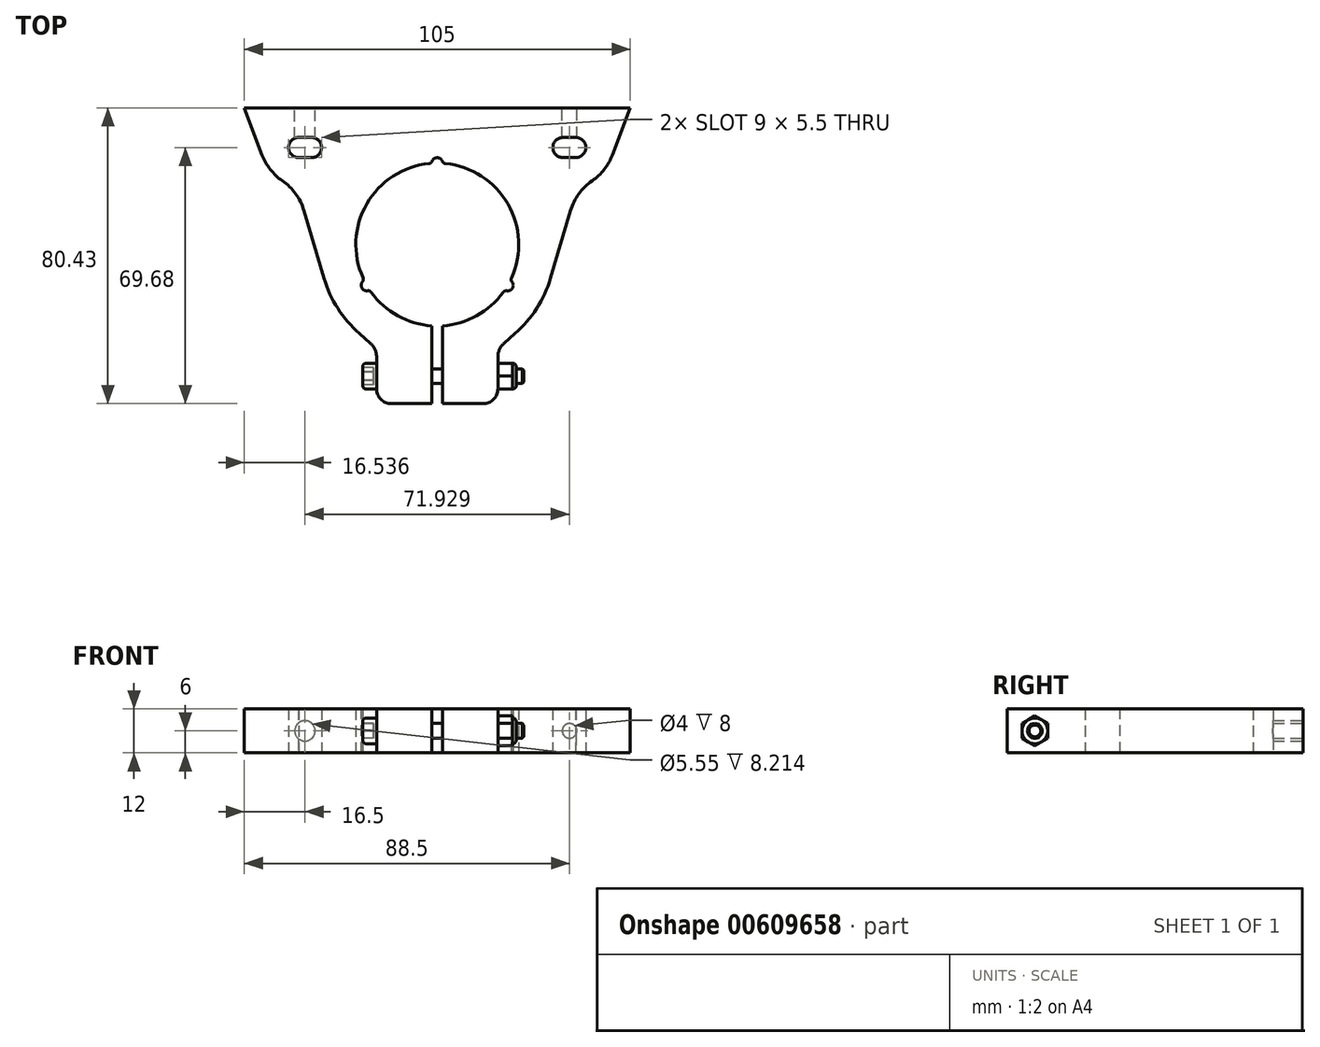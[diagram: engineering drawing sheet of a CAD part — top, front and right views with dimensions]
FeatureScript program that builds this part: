
annotation { "Feature Type Name" : "Feature", "Feature Type Description" : "" }
export const myFeature = defineFeature(function(context is Context, id is Id, definition is map)
    precondition{}
    {
        {
            var Q0;
            Q0=qCreatedBy(makeId("Top.planeOp"),FACE);
            var sketch = newSketch(context, id + "F0", { "sketchPlane" : qUnion([Q0])});
            skLineSegment(sketch, "E0", {"start": v(-52.5, 0) * mm, "end": v(52.5, 0) * mm});
            skLineSegment(sketch, "E1", {"start": v(-21.17, -61.35) * mm, "end": v(-16.5, -65.43) * mm});
            skLineSegment(sketch, "E2", {"start": v(-16.5, -65.43) * mm, "end": v(-16.5, -80.43) * mm});
            skLineSegment(sketch, "E3", {"start": v(-16.5, -80.43) * mm, "end": v(-1.5, -80.43) * mm});
            skLineSegment(sketch, "E4", {"start": v(-1.5, -80.43) * mm, "end": v(-1.5, -59.25) * mm});
            skArc(sketch, "E5", {"start": v(1.5, -59.25) * mm, "mid": v(0, -15) * mm, "end": v(-1.5, -59.25) * mm});
            skLineSegment(sketch, "E6.MirrorCS", {"start": v(16.5, -65.43) * mm, "end": v(16.5, -80.43) * mm});
            skLineSegment(sketch, "E7.MirrorCS", {"start": v(16.5, -80.43) * mm, "end": v(1.5, -80.43) * mm});
            skLineSegment(sketch, "E8.MirrorCS", {"start": v(1.5, -80.43) * mm, "end": v(1.5, -59.25) * mm});
            skCircle(sketch, "E9", {"center": v(0, -37.15) * mm, "radius": 32.15 * mm, "construction": true});
            skLineSegment(sketch, "E10", {"start": v(0, -37.15) * mm, "end": v(-21.17, -61.35) * mm, "construction": true});
            skLineSegment(sketch, "E11.bottom", {"start": v(-37.64, -13.5) * mm, "end": v(-34.21, -13.5) * mm});
            skLineSegment(sketch, "E11.top", {"start": v(-37.79, -8) * mm, "end": v(-34.21, -8) * mm});
            skArc(sketch, "E12", {"start": v(-37.79, -8) * mm, "mid": v(-40.46, -10.82) * mm, "end": v(-37.64, -13.5) * mm});
            skArc(sketch, "E13", {"start": v(-34.21, -13.5) * mm, "mid": v(-31.46, -10.75) * mm, "end": v(-34.21, -8) * mm});
            skLineSegment(sketch, "E14", {"start": v(0, 0) * mm, "end": v(0, -15) * mm, "construction": true});
            skLineSegment(sketch, "E15.MirrorCS", {"start": v(37.64, -13.5) * mm, "end": v(34.21, -13.5) * mm});
            skArc(sketch, "E16.MirrorCS", {"start": v(34.21, -13.5) * mm, "mid": v(31.46, -10.75) * mm, "end": v(34.21, -8) * mm});
            skArc(sketch, "E17.MirrorCS", {"start": v(37.79, -8) * mm, "mid": v(40.46, -10.82) * mm, "end": v(37.64, -13.5) * mm});
            skLineSegment(sketch, "E18.MirrorCS", {"start": v(37.79, -8) * mm, "end": v(34.21, -8) * mm});
            skArc(sketch, "E19.0", {"start": v(-47.67, -12.75) * mm, "mid": v(-45.45, -16.69) * mm, "end": v(-42.16, -19.79) * mm});
            skLineSegment(sketch, "E20", {"start": v(-52.5, 0) * mm, "end": v(-47.67, -12.75) * mm});
            skLineSegment(sketch, "E21", {"start": v(-36.3, -27.87) * mm, "end": v(-30.82, -46.3) * mm});
            skArc(sketch, "E22.MirrorCS", {"start": v(47.67, -12.75) * mm, "mid": v(45.45, -16.69) * mm, "end": v(42.16, -19.79) * mm});
            skLineSegment(sketch, "E23.MirrorCS", {"start": v(52.5, 0) * mm, "end": v(47.67, -12.75) * mm});
            skArc(sketch, "E24", {"start": v(-21.17, -61.35) * mm, "mid": v(-27.06, -54.5) * mm, "end": v(-30.82, -46.3) * mm});
            skLineSegment(sketch, "E25.MirrorCS", {"start": v(36.3, -27.87) * mm, "end": v(30.82, -46.3) * mm});
            skArc(sketch, "E26.MirrorCS", {"start": v(21.17, -61.35) * mm, "mid": v(27.06, -54.5) * mm, "end": v(30.82, -46.3) * mm});
            skLineSegment(sketch, "E27.MirrorCS", {"start": v(21.17, -61.35) * mm, "end": v(16.5, -65.43) * mm});
            skPoint(sketch, "E28.visualSharp", {"position": v(-38.1, -21.76) * mm});
            skArc(sketch, "E28.filletArc", {"start": v(-36.3, -27.87) * mm, "mid": v(-38.53, -23.32) * mm, "end": v(-42.16, -19.79) * mm});
            skPoint(sketch, "E29.visualSharp", {"position": v(38.1, -21.76) * mm});
            skArc(sketch, "E29.filletArc", {"start": v(42.16, -19.79) * mm, "mid": v(38.53, -23.32) * mm, "end": v(36.3, -27.87) * mm});
            skSolve(sketch);
        }
        {
            var Q0;
            Q0=qSketchRegion(id+"F0",true);
            extrude(context, id + "F1", {"entities" : qUnion([Q0]), "depth" : 12 * mm, "offsetDistance" : 25 * mm});
        }
        {
            var Q0;
            Q0=makeQuery(id+"F1.opExtrude","SWEPT_EDGE",EDGE,{"disambiguationData":[OSD([sQuery(id+"F0.wireOp",EDGE,"E1"),sQuery(id+"F0.wireOp",EDGE,"E2")])]});
            var Q1;
            Q1=makeQuery(id+"F1.opExtrude","SWEPT_EDGE",EDGE,{"disambiguationData":[OSD([sQuery(id+"F0.wireOp",EDGE,"E6.MirrorCS"),sQuery(id+"F0.wireOp",EDGE,"E27.MirrorCS")])]});
            fillet(context, id + "F2", {"entities" : qUnion([Q0, Q1]), "radius" : 5 * mm, "tangentPropagation" : true, "allowEdgeOverflow" : false});
        }
        {
            var Q0;
            Q0=makeQuery(id+"F1.opExtrude","SWEPT_FACE",FACE,{"disambiguationData":[OSD([sQuery(id+"F0.wireOp",EDGE,"E2")])]});
            var sketch = newSketch(context, id + "F3", { "sketchPlane" : qUnion([Q0])});
            skCircle(sketch, "E30", {"center": v(72.93, 6) * mm, "radius": 2 * mm});
            skPoint(sketch, "E30.centerSnap0", {"position": v(80.43, 6) * mm});
            skSolve(sketch);
        }
        {
            var Q0;
            Q0=qSketchRegion(id+"F3",true);
            extrude(context, id + "F4", {"entities" : qUnion([Q0]), "operationType" : NewBodyOperationType.REMOVE, "endBound" : BoundingType.THROUGH_ALL, "oppositeDirection" : true, "depth" : 25 * mm, "offsetDistance" : 25 * mm});
        }
        {
            var Q0;
            Q0=makeQuery(id+"F1.opExtrude","SWEPT_EDGE",EDGE,{"disambiguationData":[OSD([sQuery(id+"F0.wireOp",EDGE,"E1"),sQuery(id+"F0.wireOp",EDGE,"E2")])]});
            var Q1;
            Q1=makeQuery(id+"F1.opExtrude","SWEPT_EDGE",EDGE,{"disambiguationData":[OSD([sQuery(id+"F0.wireOp",EDGE,"E2"),sQuery(id+"F0.wireOp",EDGE,"E3")])]});
            var Q2;
            Q2=makeQuery(id+"F1.opExtrude","SWEPT_EDGE",EDGE,{"disambiguationData":[OSD([sQuery(id+"F0.wireOp",EDGE,"E6.MirrorCS"),sQuery(id+"F0.wireOp",EDGE,"E7.MirrorCS")])]});
            var Q3;
            Q3=makeQuery(id+"F1.opExtrude","SWEPT_EDGE",EDGE,{"disambiguationData":[OSD([sQuery(id+"F0.wireOp",EDGE,"6f19a3d9-82da-4a62-acf6-6007c0667a970.MirrorCS"),sQuery(id+"F0.wireOp",EDGE,"E6.MirrorCS")])]});
            fillet(context, id + "F5", {"entities" : qUnion([Q0, Q1, Q2, Q3]), "radius" : 4 * mm, "tangentPropagation" : true, "allowEdgeOverflow" : false});
        }
        {
            var Q0;
            Q0=makeQuery(id+"F1.opExtrude","SWEPT_FACE",FACE,{"disambiguationData":[OSD([sQuery(id+"F0.wireOp",EDGE,"E2")])]});
            var sketch = newSketch(context, id + "F6", { "sketchPlane" : qUnion([Q0])});
            skCircle(sketch, "E31", {"center": v(72.93, 6) * mm, "radius": 3.5 * mm});
            skSolve(sketch);
        }
        {
            var Q0;
            Q0=qSketchRegion(id+"F6",true);
            extrude(context, id + "F7", {"entities" : qUnion([Q0]), "depth" : 3.8 * mm, "offsetDistance" : 25 * mm});
        }
        {
            var Q0;
            Q0=makeQuery(id+"F7.opExtrude","CAP_FACE",FACE,{"disambiguationData":[OSD([sQuery(id+"F6.wireOp",EDGE,"E31")])],"isStart":true});
            var sketch = newSketch(context, id + "F8", { "sketchPlane" : qUnion([Q0])});
            skCircle(sketch, "E32", {"center": v(-72.93, 6) * mm, "radius": 2 * mm});
            skSolve(sketch);
        }
        {
            var Q0;
            Q0=qSketchRegion(id+"F8",true);
            extrude(context, id + "F9", {"entities" : qUnion([Q0]), "operationType" : NewBodyOperationType.ADD, "depth" : 40 * mm, "offsetDistance" : 25 * mm});
        }
        {
            var Q0;
            Q0=makeQuery(id+"F1.opExtrude","SWEPT_FACE",FACE,{"disambiguationData":[OSD([sQuery(id+"F0.wireOp",EDGE,"E6.MirrorCS")])]});
            var sketch = newSketch(context, id + "F10", { "sketchPlane" : qUnion([Q0])});
            skCircle(sketch, "E33.cCircle", {"center": v(-72.93, 6) * mm, "radius": 3.5 * mm, "construction": true});
            skLineSegment(sketch, "E33.0", {"start": v(-72.94, 1.96) * mm, "end": v(-76.44, 4) * mm});
            skLineSegment(sketch, "E33.1", {"start": v(-76.44, 4) * mm, "end": v(-76.42, 8.03) * mm});
            skLineSegment(sketch, "E33.2", {"start": v(-76.42, 8.03) * mm, "end": v(-72.92, 10.04) * mm});
            skLineSegment(sketch, "E33.3", {"start": v(-72.92, 10.04) * mm, "end": v(-69.42, 8) * mm});
            skLineSegment(sketch, "E33.4", {"start": v(-69.42, 8) * mm, "end": v(-69.44, 3.97) * mm});
            skLineSegment(sketch, "E33.5", {"start": v(-69.44, 3.97) * mm, "end": v(-72.94, 1.96) * mm});
            skPoint(sketch, "E33.0.midPoint", {"position": v(-74.7, 2.97) * mm});
            skCircle(sketch, "E34", {"center": v(-72.93, 6) * mm, "radius": 2 * mm});
            skSolve(sketch);
        }
        {
            var Q0;
            Q0=qSketchRegion(id+"F10",true);
            extrude(context, id + "F11", {"entities" : qUnion([Q0]), "depth" : 4 * mm, "offsetDistance" : 25 * mm});
        }
        {
            var Q0;
            Q0=makeQuery(id+"F11.opExtrude","CAP_FACE",FACE,{"disambiguationData":[OSD([sQuery(id+"F10.wireOp",EDGE,"E33.0"),sQuery(id+"F10.wireOp",EDGE,"E33.1"),sQuery(id+"F10.wireOp",EDGE,"E33.2"),sQuery(id+"F10.wireOp",EDGE,"E33.3"),sQuery(id+"F10.wireOp",EDGE,"E33.4"),sQuery(id+"F10.wireOp",EDGE,"E33.5"),sQuery(id+"F10.wireOp",EDGE,"E34")])],"isStart":false});
            var sketch = newSketch(context, id + "F12", { "sketchPlane" : qUnion([Q0])});
            skCircle(sketch, "E35", {"center": v(-72.93, 6) * mm, "radius": 3.5 * mm});
            skCircle(sketch, "E36", {"center": v(-72.93, 6) * mm, "radius": 2 * mm});
            skSolve(sketch);
        }
        {
            var Q0;
            Q0=qSketchRegion(id+"F12",true);
            extrude(context, id + "F13", {"entities" : qUnion([Q0]), "operationType" : NewBodyOperationType.ADD, "depth" : 1 * mm, "offsetDistance" : 25 * mm});
        }
        {
            var Q0;
            {var subQ0=sQuery(id+"F12.wireOp",EDGE,"E35");var subQ1=makeQuery(id+"F11.opExtrude","CAP_EDGE",EDGE,{"disambiguationData":[OSD([sQuery(id+"F10.wireOp",EDGE,"E33.4")])],"isStart":false});var subQ2=makeQuery(id+"F12.imprint","INTERSECT",VERTEX,{"derivedFrom":[makeQuery(id+"F11.opExtrude","CAP_EDGE",EDGE,{"disambiguationData":[OSD([sQuery(id+"F10.wireOp",EDGE,"E33.5")])],"isStart":false}),subQ0]});var subQ3=makeQuery(id+"F12.imprint","INTERSECT",VERTEX,{"derivedFrom":[makeQuery(id+"F11.opExtrude","CAP_EDGE",EDGE,{"disambiguationData":[OSD([sQuery(id+"F10.wireOp",EDGE,"E33.0")])],"isStart":false}),subQ0]});var subQ4=makeQuery(id+"F12.imprint","INTERSECT",VERTEX,{"derivedFrom":[makeQuery(id+"F11.opExtrude","CAP_EDGE",EDGE,{"disambiguationData":[OSD([sQuery(id+"F10.wireOp",EDGE,"E33.1")])],"isStart":false}),subQ0]});var subQ5=makeQuery(id+"F12.imprint","INTERSECT",VERTEX,{"derivedFrom":[makeQuery(id+"F11.opExtrude","CAP_EDGE",EDGE,{"disambiguationData":[OSD([sQuery(id+"F10.wireOp",EDGE,"E33.2")])],"isStart":false}),subQ0]});var subQ6=makeQuery(id+"F12.imprint","INTERSECT",VERTEX,{"derivedFrom":[makeQuery(id+"F11.opExtrude","CAP_EDGE",EDGE,{"disambiguationData":[OSD([sQuery(id+"F10.wireOp",EDGE,"E33.3")])],"isStart":false}),subQ0]});Q0=makeQuery(id+"F13.opExtrude","CAP_EDGE",EDGE,{"disambiguationData":[OSD([subQ0]),TDD([makeQuery(id+"F12.imprint","IMPRINT",EDGE,{"disambiguationData":[TD([[makeQuery(id+"F12.imprint","INTERSECT",VERTEX,{"disambiguationData":[OD(0.0)],"derivedFrom":[subQ1,subQ0]}),-1.0],[subQ6,1.0]])],"derivedFrom":subQ0}),makeQuery(id+"F12.imprint","IMPRINT",EDGE,{"disambiguationData":[TD([[subQ6,-1.0],[subQ5,1.0]])],"derivedFrom":subQ0}),makeQuery(id+"F12.imprint","IMPRINT",EDGE,{"disambiguationData":[TD([[subQ5,-1.0],[subQ4,1.0]])],"derivedFrom":subQ0}),makeQuery(id+"F12.imprint","IMPRINT",EDGE,{"disambiguationData":[TD([[subQ4,-1.0],[subQ3,1.0]])],"derivedFrom":subQ0}),makeQuery(id+"F12.imprint","IMPRINT",EDGE,{"disambiguationData":[TD([[subQ3,-1.0],[subQ2,1.0]])],"derivedFrom":subQ0}),makeQuery(id+"F12.imprint","IMPRINT",EDGE,{"disambiguationData":[TD([[makeQuery(id+"F12.imprint","INTERSECT",VERTEX,{"disambiguationData":[OD(1.0)],"derivedFrom":[subQ1,subQ0]}),1.0],[subQ2,-1.0]])],"derivedFrom":subQ0})])],"isStart":false});}
            fillet(context, id + "F14", {"entities" : qUnion([Q0]), "radius" : 1 * mm, "tangentPropagation" : true, "allowEdgeOverflow" : false});
        }
        {
            var Q0;
            Q0=makeQuery(id+"F9.opExtrude","CAP_EDGE",EDGE,{"disambiguationData":[OSD([sQuery(id+"F8.wireOp",EDGE,"E32")])],"isStart":false});
            chamfer(context, id + "F15", {"entities" : qUnion([Q0]), "width" : 0.4 * mm, "tangentPropagation" : true});
        }
        {
            var Q0;
            Q0=makeQuery(id+"F7.opExtrude","CAP_FACE",FACE,{"disambiguationData":[OSD([sQuery(id+"F6.wireOp",EDGE,"E31")])],"isStart":false});
            var sketch = newSketch(context, id + "F16", { "sketchPlane" : qUnion([Q0])});
            skCircle(sketch, "E37.cCircle", {"center": v(72.93, 6) * mm, "radius": 2 * mm, "construction": true});
            skLineSegment(sketch, "E37.0", {"start": v(75.24, 5.9) * mm, "end": v(74, 3.95) * mm});
            skLineSegment(sketch, "E37.1", {"start": v(74, 3.95) * mm, "end": v(71.68, 4.06) * mm});
            skLineSegment(sketch, "E37.2", {"start": v(71.68, 4.06) * mm, "end": v(70.62, 6.1) * mm});
            skLineSegment(sketch, "E37.3", {"start": v(70.62, 6.1) * mm, "end": v(71.87, 8.05) * mm});
            skLineSegment(sketch, "E37.4", {"start": v(71.87, 8.05) * mm, "end": v(74.18, 7.94) * mm});
            skLineSegment(sketch, "E37.5", {"start": v(74.18, 7.94) * mm, "end": v(75.24, 5.9) * mm});
            skPoint(sketch, "E37.0.midPoint", {"position": v(74.61, 4.92) * mm});
            skSolve(sketch);
        }
        {
            var Q0;
            Q0=qSketchRegion(id+"F16",true);
            extrude(context, id + "F17", {"entities" : qUnion([Q0]), "operationType" : NewBodyOperationType.REMOVE, "oppositeDirection" : true, "depth" : 3 * mm, "offsetDistance" : 25 * mm});
        }
        {
            var Q0;
            Q0=makeQuery(id+"F7.opExtrude","CAP_EDGE",EDGE,{"disambiguationData":[OSD([sQuery(id+"F6.wireOp",EDGE,"E31")])],"isStart":false});
            fillet(context, id + "F18", {"entities" : qUnion([Q0]), "radius" : 1 * mm, "tangentPropagation" : true, "allowEdgeOverflow" : false});
        }
        {
            var Q0;
            Q0=makeQuery(id+"F1.opExtrude","SWEPT_FACE",FACE,{"disambiguationData":[OSD([sQuery(id+"F0.wireOp",EDGE,"E0")])]});
            var sketch = newSketch(context, id + "F19", { "sketchPlane" : qUnion([Q0])});
            skCircle(sketch, "E38", {"center": v(-36, 6) * mm, "radius": 2 * mm});
            skPoint(sketch, "E38.centerSnap0", {"position": v(-52.5, 6) * mm});
            skCircle(sketch, "E39", {"center": v(36, 6) * mm, "radius": 2.77 * mm});
            skSolve(sketch);
        }
        {
            var Q0;
            Q0 = qSketchRegion(id + "F19", true);
            extrude(context, id + "F20", {"entities" : qUnion([Q0]), "operationType" : NewBodyOperationType.REMOVE, "oppositeDirection" : true, "depth" : 12 * mm, "offsetDistance" : 25 * mm});
        }
        {
            var Q0;
            Q0=makeQuery(id+"F1.opExtrude","CAP_FACE",FACE,{"disambiguationData":[OSD([sQuery(id+"F0.wireOp",EDGE,"E0"),sQuery(id+"F0.wireOp",EDGE,"E1"),sQuery(id+"F0.wireOp",EDGE,"E2"),sQuery(id+"F0.wireOp",EDGE,"E3"),sQuery(id+"F0.wireOp",EDGE,"E4"),sQuery(id+"F0.wireOp",EDGE,"E5"),sQuery(id+"F0.wireOp",EDGE,"E6.MirrorCS"),sQuery(id+"F0.wireOp",EDGE,"E7.MirrorCS"),sQuery(id+"F0.wireOp",EDGE,"E8.MirrorCS"),sQuery(id+"F0.wireOp",EDGE,"E11.bottom"),sQuery(id+"F0.wireOp",EDGE,"E11.top"),sQuery(id+"F0.wireOp",EDGE,"E12"),sQuery(id+"F0.wireOp",EDGE,"E13"),sQuery(id+"F0.wireOp",EDGE,"E15.MirrorCS"),sQuery(id+"F0.wireOp",EDGE,"E16.MirrorCS"),sQuery(id+"F0.wireOp",EDGE,"E17.MirrorCS"),sQuery(id+"F0.wireOp",EDGE,"E18.MirrorCS"),sQuery(id+"F0.wireOp",EDGE,"E19.0"),sQuery(id+"F0.wireOp",EDGE,"E20"),sQuery(id+"F0.wireOp",EDGE,"E21"),sQuery(id+"F0.wireOp",EDGE,"E22.MirrorCS"),sQuery(id+"F0.wireOp",EDGE,"E23.MirrorCS"),sQuery(id+"F0.wireOp",EDGE,"E24"),sQuery(id+"F0.wireOp",EDGE,"E25.MirrorCS"),sQuery(id+"F0.wireOp",EDGE,"E26.MirrorCS"),sQuery(id+"F0.wireOp",EDGE,"E27.MirrorCS"),sQuery(id+"F0.wireOp",EDGE,"E28.filletArc"),sQuery(id+"F0.wireOp",EDGE,"E29.filletArc")])],"isStart":false});
            var sketch = newSketch(context, id + "F21", { "sketchPlane" : qUnion([Q0])});
            skCircle(sketch, "E40", {"center": v(0, -15) * mm, "radius": 1.5 * mm});
            skCircle(sketch, "E41.1.0", {"center": v(-19.18, -48.22) * mm, "radius": 1.5 * mm});
            skCircle(sketch, "E41.2.0", {"center": v(19.18, -48.23) * mm, "radius": 1.5 * mm});
            skPoint(sketch, "E41.center", {"position": v(0, -37.15) * mm});
            skSolve(sketch);
        }
        {
            var Q0;
            Q0 = qSketchRegion(id + "F21", true);
            extrude(context, id + "F22", {"entities" : qUnion([Q0]), "operationType" : NewBodyOperationType.REMOVE, "oppositeDirection" : true, "depth" : 25 * mm, "offsetDistance" : 25 * mm});
        }
        {
            var Q0;
            Q0=makeQuery(id+"F22.boolean.opBoolean","INTERSECT",EDGE,{"disambiguationData":[OD(1.0)],"derivedFrom":[makeQuery(id+"F1.opExtrude","SWEPT_FACE",FACE,{"disambiguationData":[OSD([sQuery(id+"F0.wireOp",EDGE,"E5")])]}),makeQuery(id+"F22.opExtrude","SWEPT_FACE",FACE,{"disambiguationData":[OSD([sQuery(id+"F21.wireOp",EDGE,"E40")])]})]});
            var Q1;
            Q1=makeQuery(id+"F22.boolean.opBoolean","INTERSECT",EDGE,{"disambiguationData":[OD(0.0)],"derivedFrom":[makeQuery(id+"F1.opExtrude","SWEPT_FACE",FACE,{"disambiguationData":[OSD([sQuery(id+"F0.wireOp",EDGE,"E5")])]}),makeQuery(id+"F22.opExtrude","SWEPT_FACE",FACE,{"disambiguationData":[OSD([sQuery(id+"F21.wireOp",EDGE,"E40")])]})]});
            var Q2;
            Q2=makeQuery(id+"F22.boolean.opBoolean","INTERSECT",EDGE,{"disambiguationData":[OD(1.0)],"derivedFrom":[makeQuery(id+"F1.opExtrude","SWEPT_FACE",FACE,{"disambiguationData":[OSD([sQuery(id+"F0.wireOp",EDGE,"E5")])]}),makeQuery(id+"F22.opExtrude","SWEPT_FACE",FACE,{"disambiguationData":[OSD([sQuery(id+"F21.wireOp",EDGE,"E41.1.0")])]})]});
            var Q3;
            Q3=makeQuery(id+"F22.boolean.opBoolean","INTERSECT",EDGE,{"disambiguationData":[OD(0.0)],"derivedFrom":[makeQuery(id+"F1.opExtrude","SWEPT_FACE",FACE,{"disambiguationData":[OSD([sQuery(id+"F0.wireOp",EDGE,"E5")])]}),makeQuery(id+"F22.opExtrude","SWEPT_FACE",FACE,{"disambiguationData":[OSD([sQuery(id+"F21.wireOp",EDGE,"E41.1.0")])]})]});
            var Q4;
            Q4=makeQuery(id+"F22.boolean.opBoolean","INTERSECT",EDGE,{"disambiguationData":[OD(0.0)],"derivedFrom":[makeQuery(id+"F1.opExtrude","SWEPT_FACE",FACE,{"disambiguationData":[OSD([sQuery(id+"F0.wireOp",EDGE,"E5")])]}),makeQuery(id+"F22.opExtrude","SWEPT_FACE",FACE,{"disambiguationData":[OSD([sQuery(id+"F21.wireOp",EDGE,"E41.2.0")])]})]});
            var Q5;
            Q5=makeQuery(id+"F22.boolean.opBoolean","INTERSECT",EDGE,{"disambiguationData":[OD(1.0)],"derivedFrom":[makeQuery(id+"F1.opExtrude","SWEPT_FACE",FACE,{"disambiguationData":[OSD([sQuery(id+"F0.wireOp",EDGE,"E5")])]}),makeQuery(id+"F22.opExtrude","SWEPT_FACE",FACE,{"disambiguationData":[OSD([sQuery(id+"F21.wireOp",EDGE,"E41.2.0")])]})]});
            fillet(context, id + "F23", {"entities" : qUnion([Q0, Q1, Q2, Q3, Q4, Q5]), "radius" : 1 * mm, "tangentPropagation" : true, "allowEdgeOverflow" : false});
        }
    });
